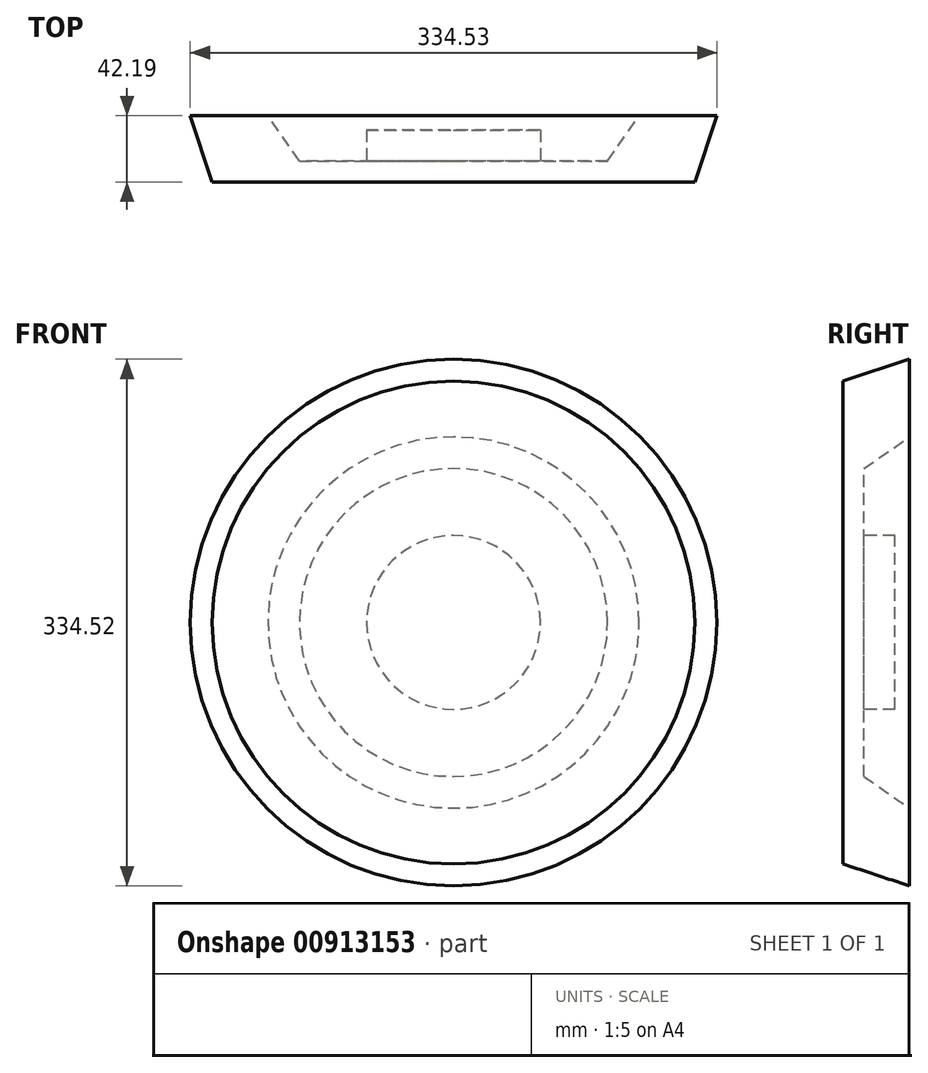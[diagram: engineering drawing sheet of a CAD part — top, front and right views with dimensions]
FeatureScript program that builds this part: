
annotation { "Feature Type Name" : "Feature", "Feature Type Description" : "" }
export const myFeature = defineFeature(function(context is Context, id is Id, definition is map)
    precondition{}
    {
        {
            var Q0;
            Q0=qCreatedBy(makeId("Top.planeOp"),FACE);
            var sketch = newSketch(context, id + "F0", { "sketchPlane" : qUnion([Q0])});
            skLineSegment(sketch, "E0", {"start": v(0, 0) * mm, "end": v(153.32, 0) * mm, "construction": true});
            skLineSegment(sketch, "E1", {"start": v(153.32, 0) * mm, "end": v(153.32, 33.04) * mm});
            skLineSegment(sketch, "E2", {"start": v(153.32, 33.04) * mm, "end": v(98.11, 33.04) * mm});
            skLineSegment(sketch, "E3", {"start": v(98.11, 33.04) * mm, "end": v(98.11, 13.43) * mm});
            skLineSegment(sketch, "E4", {"start": v(98.11, 13.43) * mm, "end": v(55.5, 13.43) * mm});
            skLineSegment(sketch, "E5", {"start": v(55.5, 13.43) * mm, "end": v(35.42, 42.19) * mm});
            skLineSegment(sketch, "E6", {"start": v(35.42, 42.19) * mm, "end": v(-13.95, 42.19) * mm});
            skLineSegment(sketch, "E7", {"start": v(-13.95, 42.19) * mm, "end": v(0, 0) * mm});
            skLineSegment(sketch, "E8", {"start": v(0, 0) * mm, "end": v(153.32, 0) * mm});
            skSolve(sketch);
        }
        {
            var Q0;
            Q0=makeQuery(id+"F0.imprint","IMPRINT",FACE,{"disambiguationData":[TD([[makeQuery(id+"F0.imprint","IMPRINT",EDGE,{"derivedFrom":sQuery(id+"F0.wireOp",EDGE,"E1")}),1.0]])]});
            var Q1;
            Q1=sQuery(id+"F0.wireOp",EDGE,"E1");
            revolve(context, id + "F1", {"surfaceOperationType" : NewSurfaceOperationType.NEW, "entities" : qUnion([Q0]), "axis" : qUnion([Q1]), "revolveType" : RevolveType.FULL});
        }
    });
